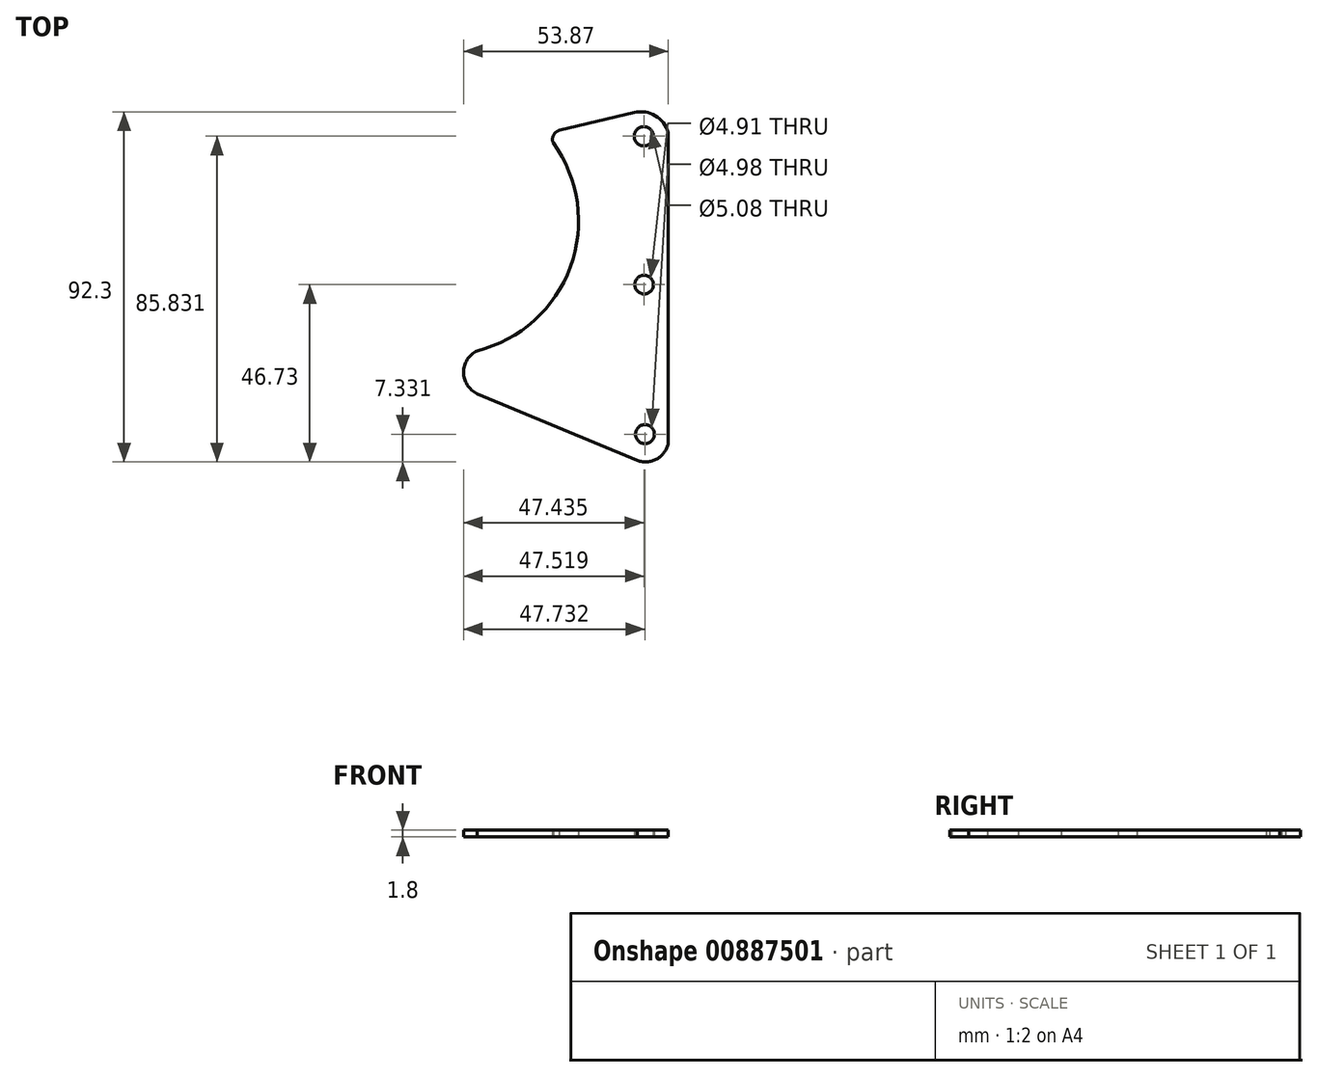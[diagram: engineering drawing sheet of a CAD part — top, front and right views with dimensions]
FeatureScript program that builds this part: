
annotation { "Feature Type Name" : "Feature", "Feature Type Description" : "" }
export const myFeature = defineFeature(function(context is Context, id is Id, definition is map)
    precondition{}
    {
        {
            var Q0;
            Q0=qCreatedBy(makeId("Top.planeOp"),FACE);
            var sketch = newSketch(context, id + "F0", { "sketchPlane" : qUnion([Q0])});
            skPoint(sketch, "E0", {"position": v(0, -80.04) * mm});
            skPoint(sketch, "E1", {"position": v(-8.1, -84.59) * mm});
            skArc(sketch, "E2", {"start": v(-8.1, -84.59) * mm, "mid": v(-2.99, -84.2) * mm, "end": v(0, -80.04) * mm});
            skPoint(sketch, "E3", {"position": v(-50.34, -66.98) * mm});
            skPoint(sketch, "E4", {"position": v(-50.34, -55.71) * mm});
            skArc(sketch, "E5", {"start": v(-50.34, -55.71) * mm, "mid": v(-53.87, -61.35) * mm, "end": v(-50.34, -66.98) * mm});
            skLineSegment(sketch, "E6", {"start": v(-50.34, -66.98) * mm, "end": v(-8.1, -84.59) * mm});
            skPoint(sketch, "E7", {"position": v(-30.3, -0.85) * mm});
            skPoint(sketch, "E8", {"position": v(-28.77, 2.37) * mm});
            skArc(sketch, "E9", {"start": v(-28.77, 2.37) * mm, "mid": v(-30.22, 1.09) * mm, "end": v(-30.3, -0.85) * mm});
            skArc(sketch, "E10", {"start": v(-50.34, -55.71) * mm, "mid": v(-25.76, -33.6) * mm, "end": v(-30.3, -0.85) * mm});
            skCircle(sketch, "E11", {"center": v(-6.35, -38.25) * mm, "radius": 2.45 * mm});
            skPoint(sketch, "E11.first.point", {"position": v(-6.4, -35.8) * mm});
            skPoint(sketch, "E11.second.point", {"position": v(-6.23, -40.7) * mm});
            skPoint(sketch, "E11.third.point", {"position": v(-8.8, -38.37) * mm});
            skCircle(sketch, "E12", {"center": v(-6.14, -77.65) * mm, "radius": 2.5 * mm});
            skPoint(sketch, "E12.first.point", {"position": v(-6.24, -75.16) * mm});
            skPoint(sketch, "E12.second.point", {"position": v(-5.96, -80.13) * mm});
            skPoint(sketch, "E12.third.point", {"position": v(-3.69, -78.1) * mm});
            skCircle(sketch, "E13", {"center": v(-6.43, 0.85) * mm, "radius": 2.54 * mm});
            skPoint(sketch, "E13.first.point", {"position": v(-6.55, 3.39) * mm});
            skPoint(sketch, "E13.second.point", {"position": v(-6.39, -1.69) * mm});
            skPoint(sketch, "E13.third.point", {"position": v(-3.9, 0.6) * mm});
            skLineSegment(sketch, "E14", {"start": v(-28.77, 2.37) * mm, "end": v(-8.95, 7.12) * mm});
            skPoint(sketch, "E15", {"position": v(0, 1.83) * mm});
            skArc(sketch, "E16", {"start": v(0, 1.83) * mm, "mid": v(-3.4, 6.28) * mm, "end": v(-8.95, 7.12) * mm});
            skLineSegment(sketch, "E17", {"start": v(0, 1.83) * mm, "end": v(0, -80.04) * mm});
            skPoint(sketch, "E18", {"position": v(-6.96, 7.32) * mm});
            skPoint(sketch, "E19", {"position": v(-5.97, -84.98) * mm});
            skSolve(sketch);
        }
        {
            var Q0;
            Q0=makeQuery(id+"F0.imprint","IMPRINT",FACE,{"disambiguationData":[TD([[makeQuery(id+"F0.imprint","IMPRINT",EDGE,{"derivedFrom":sQuery(id+"F0.wireOp",EDGE,"E2")}),1.0]])]});
            extrude(context, id + "F1", {"entities" : qUnion([Q0]), "depth" : 1.8 * mm, "offsetDistance" : 25 * mm});
        }
    });
